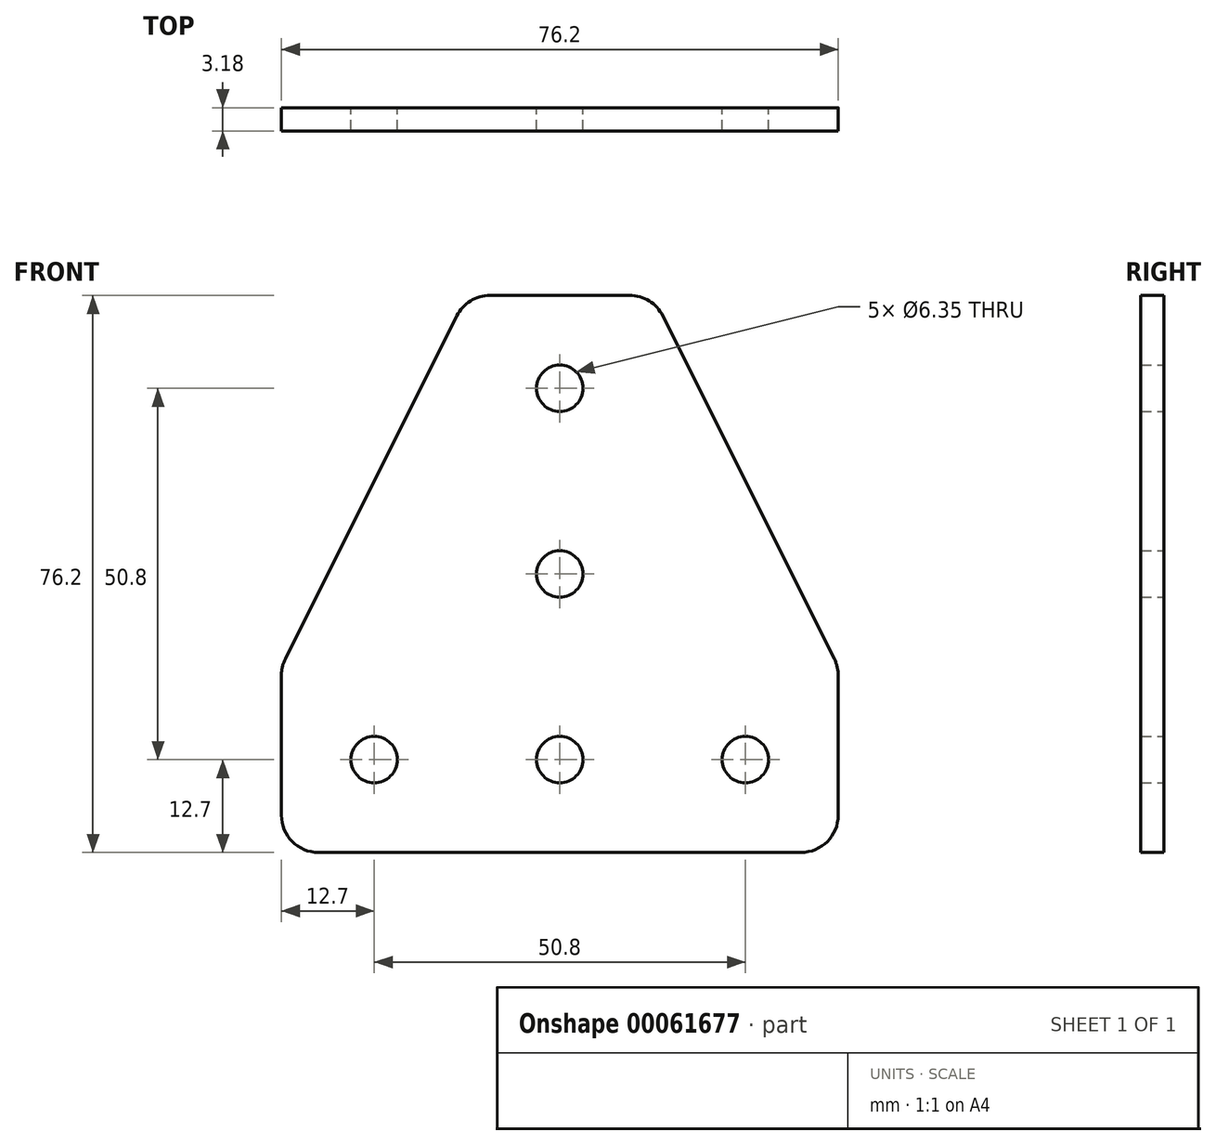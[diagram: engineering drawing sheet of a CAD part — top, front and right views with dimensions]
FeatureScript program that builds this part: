
annotation { "Feature Type Name" : "Feature", "Feature Type Description" : "" }
export const myFeature = defineFeature(function(context is Context, id is Id, definition is map)
    precondition{}
    {
        {
            var Q0;
            Q0=qCreatedBy(makeId("Front.planeOp"),FACE);
            var sketch = newSketch(context, id + "F0", { "sketchPlane" : qUnion([Q0])});
            skLineSegment(sketch, "E0.bottom", {"start": v(-38.1, 0) * mm, "end": v(38.1, 0) * mm});
            skLineSegment(sketch, "E0.top", {"start": v(-38.1, 76.2) * mm, "end": v(38.1, 76.2) * mm});
            skLineSegment(sketch, "E0.left", {"start": v(-38.1, 0) * mm, "end": v(-38.1, 76.2) * mm});
            skLineSegment(sketch, "E0.right", {"start": v(38.1, 0) * mm, "end": v(38.1, 76.2) * mm});
            skLineSegment(sketch, "E1", {"start": v(-38.1, 25.4) * mm, "end": v(-12.7, 76.2) * mm});
            skLineSegment(sketch, "E2", {"start": v(38.1, 25.4) * mm, "end": v(12.7, 76.2) * mm});
            skPoint(sketch, "E3.positionSnap0", {"position": v(0, 0) * mm});
            skSolve(sketch);
        }
        {
            var Q0;
            {var subQ1=sQuery(id+"F0.wireOp",EDGE,"E0.bottom");Q0=makeQuery(id+"F0.imprint","IMPRINT",FACE,{"disambiguationData":[TD([[makeQuery(id+"F0.imprint","IMPRINT",EDGE,{"derivedFrom":subQ1}),1.0]])]});}
            extrude(context, id + "F1", {"entities" : qUnion([Q0]), "depth" : 3.17 * mm});
        }
        {
            var Q0;
            Q0=makeQuery(id+"F1.opExtrude","SWEPT_EDGE",EDGE,{"disambiguationData":[OSD([sQuery(id+"F0.wireOp",EDGE,"E0.top"),sQuery(id+"F0.wireOp",EDGE,"E2")])]});
            var Q1;
            Q1=makeQuery(id+"F1.opExtrude","SWEPT_EDGE",EDGE,{"disambiguationData":[OSD([sQuery(id+"F0.wireOp",EDGE,"E0.top"),sQuery(id+"F0.wireOp",EDGE,"E1")])]});
            var Q2;
            Q2=makeQuery(id+"F1.opExtrude","SWEPT_EDGE",EDGE,{"disambiguationData":[OSD([sQuery(id+"F0.wireOp",EDGE,"E0.right"),sQuery(id+"F0.wireOp",EDGE,"E2")])]});
            var Q3;
            Q3=makeQuery(id+"F1.opExtrude","SWEPT_EDGE",EDGE,{"disambiguationData":[OSD([sQuery(id+"F0.wireOp",EDGE,"E0.bottom"),sQuery(id+"F0.wireOp",EDGE,"E0.right")])]});
            var Q4;
            Q4=makeQuery(id+"F1.opExtrude","SWEPT_EDGE",EDGE,{"disambiguationData":[OSD([sQuery(id+"F0.wireOp",EDGE,"E0.left"),sQuery(id+"F0.wireOp",EDGE,"E1")])]});
            var Q5;
            Q5=makeQuery(id+"F1.opExtrude","SWEPT_EDGE",EDGE,{"disambiguationData":[OSD([sQuery(id+"F0.wireOp",EDGE,"E0.bottom"),sQuery(id+"F0.wireOp",EDGE,"E0.left")])]});
            fillet(context, id + "F2", {"entities" : qUnion([Q0, Q1, Q2, Q3, Q4, Q5]), "radius" : 5.08 * mm, "tangentPropagation" : true, "allowEdgeOverflow" : false});
        }
        {
            var Q0;
            Q0=makeQuery(id+"F1.opExtrude","CAP_FACE",FACE,{"disambiguationData":[OSD([sQuery(id+"F0.wireOp",EDGE,"E0.bottom"),sQuery(id+"F0.wireOp",EDGE,"E0.top"),sQuery(id+"F0.wireOp",EDGE,"E0.left"),sQuery(id+"F0.wireOp",EDGE,"E0.right"),sQuery(id+"F0.wireOp",EDGE,"E1"),sQuery(id+"F0.wireOp",EDGE,"E2")])],"isStart":true});
            var sketch = newSketch(context, id + "F3", { "sketchPlane" : qUnion([Q0])});
            skPoint(sketch, "E4", {"position": v(0, 12.7) * mm});
            skPoint(sketch, "E4.positionSnap0", {"position": v(0, 0) * mm});
            skPoint(sketch, "E5", {"position": v(-25.4, 12.7) * mm});
            skPoint(sketch, "E6", {"position": v(25.4, 12.7) * mm});
            skPoint(sketch, "E7", {"position": v(0, 38.1) * mm});
            skPoint(sketch, "E8", {"position": v(0, 63.5) * mm});
            skSolve(sketch);
        }
        {
            var Q0;
            Q0=sQuery(id+"F3.wireOp",VERTEX,"E5");
            var Q1;
            Q1=sQuery(id+"F3.wireOp",VERTEX,"E4");
            var Q2;
            Q2=sQuery(id+"F3.wireOp",VERTEX,"E6");
            var Q3;
            Q3=sQuery(id+"F3.wireOp",VERTEX,"E7");
            var Q4;
            Q4=sQuery(id+"F3.wireOp",VERTEX,"E8");
            var Q5;
            Q5=makeQuery(id+"F1.opExtrude","SWEPT_BODY",BODY,{"disambiguationData":[OSD([sQuery(id+"F0.wireOp",EDGE,"E0.bottom"),sQuery(id+"F0.wireOp",EDGE,"E0.top"),sQuery(id+"F0.wireOp",EDGE,"E0.left"),sQuery(id+"F0.wireOp",EDGE,"E0.right"),sQuery(id+"F0.wireOp",EDGE,"E1"),sQuery(id+"F0.wireOp",EDGE,"E2")])]});
            hole(context, id + "F4", {"style" : HoleStyle.SIMPLE, "holeDiameter" : 6.35 * mm, "endStyle" : HoleEndStyle.THROUGH, "locations" : qUnion([Q0, Q1, Q2, Q3, Q4]), "scope" : qUnion([Q5])});
        }
    });
